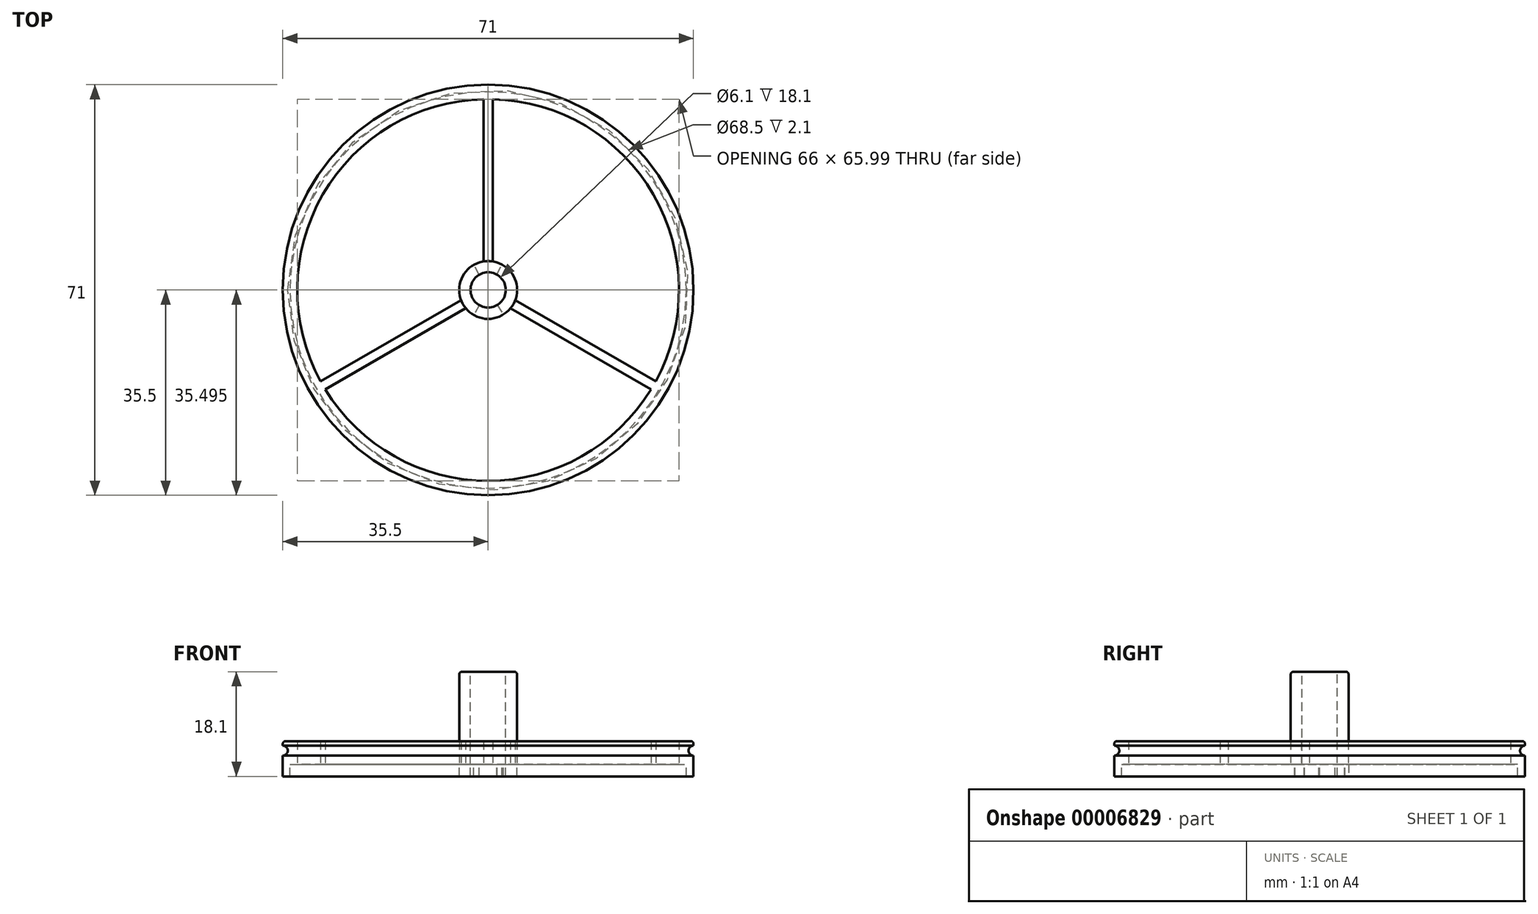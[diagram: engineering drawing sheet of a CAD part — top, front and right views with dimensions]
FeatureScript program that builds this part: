
annotation { "Feature Type Name" : "Feature", "Feature Type Description" : "" }
export const myFeature = defineFeature(function(context is Context, id is Id, definition is map)
    precondition{}
    {
        {
            var Q0;
            Q0=qCreatedBy(makeId("Top.planeOp"),FACE);
            var sketch = newSketch(context, id + "F0", { "sketchPlane" : qUnion([Q0])});
            skCircle(sketch, "E0", {"center": v(0, 0) * mm, "radius": 5 * mm});
            skCircle(sketch, "E1", {"center": v(0, 0) * mm, "radius": 33 * mm});
            skLineSegment(sketch, "E2", {"start": v(-0.81, 4.93) * mm, "end": v(-0.81, 33) * mm});
            skLineSegment(sketch, "E3.0.MirrorCS", {"start": v(0.81, 4.93) * mm, "end": v(0.81, 33) * mm});
            skLineSegment(sketch, "E4.1.0", {"start": v(-4.68, -1.76) * mm, "end": v(-28.98, -15.8) * mm});
            skLineSegment(sketch, "E4.1.1", {"start": v(-3.87, -3.17) * mm, "end": v(-28.16, -17.2) * mm});
            skLineSegment(sketch, "E4.2.0", {"start": v(3.87, -3.17) * mm, "end": v(28.16, -17.2) * mm});
            skLineSegment(sketch, "E4.2.1", {"start": v(4.68, -1.76) * mm, "end": v(28.98, -15.8) * mm});
            skCircle(sketch, "E5", {"center": v(0, 0) * mm, "radius": 35.5 * mm});
            skSolve(sketch);
        }
        {
            var Q0;
            Q0=makeQuery(id+"F0.imprint","IMPRINT",FACE,{"disambiguationData":[TD([[makeQuery(id+"F0.imprint","IMPRINT",EDGE,{"derivedFrom":sQuery(id+"F0.wireOp",EDGE,"E5")}),1.0]])]});
            var Q1;
            {var subQ1=sQuery(id+"F0.wireOp",EDGE,"E2");Q1=makeQuery(id+"F0.imprint","IMPRINT",FACE,{"disambiguationData":[TD([[makeQuery(id+"F0.imprint","IMPRINT",EDGE,{"derivedFrom":subQ1}),-1.0]])]});}
            var Q2;
            {var subQ0=sQuery(id+"F0.wireOp",EDGE,"E4.2.0");Q2=makeQuery(id+"F0.imprint","IMPRINT",FACE,{"disambiguationData":[TD([[makeQuery(id+"F0.imprint","IMPRINT",EDGE,{"derivedFrom":subQ0}),1.0]])]});}
            var Q3;
            {var subQ0=sQuery(id+"F0.wireOp",EDGE,"E4.1.0");Q3=makeQuery(id+"F0.imprint","IMPRINT",FACE,{"disambiguationData":[TD([[makeQuery(id+"F0.imprint","IMPRINT",EDGE,{"derivedFrom":subQ0}),1.0]])]});}
            var Q4;
            {var subQ0=sQuery(id+"F0.wireOp",EDGE,"E0");var subQ6=makeQuery(id+"F0.imprint","INTERSECT",VERTEX,{"derivedFrom":[subQ0,sQuery(id+"F0.wireOp",EDGE,"E2")]});Q4=makeQuery(id+"F0.imprint","IMPRINT",FACE,{"disambiguationData":[TD([[makeQuery(id+"F0.imprint","IMPRINT",EDGE,{"disambiguationData":[TD([[subQ6,1.0]])],"derivedFrom":subQ0}),1.0]])]});}
            extrude(context, id + "F1", {"entities" : qUnion([Q0, Q1, Q2, Q3, Q4]), "depth" : 4 * mm});
        }
        {
            var Q0;
            Q0=makeQuery(id+"F1.opExtrude","CAP_FACE",FACE,{"disambiguationData":[OSD([sQuery(id+"F0.wireOp",EDGE,"E0"),sQuery(id+"F0.wireOp",EDGE,"E1"),sQuery(id+"F0.wireOp",EDGE,"E2"),sQuery(id+"F0.wireOp",EDGE,"E3.0.MirrorCS"),sQuery(id+"F0.wireOp",EDGE,"E4.1.0"),sQuery(id+"F0.wireOp",EDGE,"E4.1.1"),sQuery(id+"F0.wireOp",EDGE,"E4.2.0"),sQuery(id+"F0.wireOp",EDGE,"E4.2.1"),sQuery(id+"F0.wireOp",EDGE,"E5")])],"isStart":false});
            var sketch = newSketch(context, id + "F2", { "sketchPlane" : qUnion([Q0])});
            skCircle(sketch, "E6", {"center": v(0, 0) * mm, "radius": 5 * mm});
            skSolve(sketch);
        }
        {
            var Q0;
            Q0 = qSketchRegion(id + "F2", true);
            extrude(context, id + "F3", {"entities" : qUnion([Q0]), "operationType" : NewBodyOperationType.ADD, "depth" : 12 * mm});
        }
        {
            var Q0;
            Q0=makeQuery(id+"F3.opExtrude","CAP_FACE",FACE,{"disambiguationData":[OSD([sQuery(id+"F2.wireOp",EDGE,"E6")])],"isStart":false});
            var sketch = newSketch(context, id + "F4", { "sketchPlane" : qUnion([Q0])});
            skCircle(sketch, "E7", {"center": v(0, 0) * mm, "radius": 3.05 * mm});
            skSolve(sketch);
        }
        {
            var Q0;
            Q0 = qSketchRegion(id + "F4", true);
            extrude(context, id + "F5", {"entities" : qUnion([Q0]), "operationType" : NewBodyOperationType.REMOVE, "endBound" : BoundingType.UP_TO_NEXT, "oppositeDirection" : true, "depth" : 25 * mm});
        }
        {
            var Q0;
            Q0=makeQuery(id+"F3.opExtrude","CAP_EDGE",EDGE,{"disambiguationData":[OSD([sQuery(id+"F2.wireOp",EDGE,"E6")])],"isStart":false});
            var Q1;
            Q1=makeQuery(id+"F1.opExtrude","CAP_EDGE",EDGE,{"disambiguationData":[OSD([sQuery(id+"F0.wireOp",EDGE,"E5")])],"isStart":false});
            fillet(context, id + "F6", {"entities" : qUnion([Q0, Q1]), "radius" : .5 * mm, "tangentPropagation" : true, "allowEdgeOverflow" : false});
        }
        {
            var Q0;
            Q0=makeQuery(id+"F1.opExtrude","CAP_FACE",FACE,{"disambiguationData":[OSD([sQuery(id+"F0.wireOp",EDGE,"E0"),sQuery(id+"F0.wireOp",EDGE,"E1"),sQuery(id+"F0.wireOp",EDGE,"E2"),sQuery(id+"F0.wireOp",EDGE,"E3.0.MirrorCS"),sQuery(id+"F0.wireOp",EDGE,"E4.1.0"),sQuery(id+"F0.wireOp",EDGE,"E4.1.1"),sQuery(id+"F0.wireOp",EDGE,"E4.2.0"),sQuery(id+"F0.wireOp",EDGE,"E4.2.1"),sQuery(id+"F0.wireOp",EDGE,"E5")])],"isStart":true});
            var sketch = newSketch(context, id + "F7", { "sketchPlane" : qUnion([Q0])});
            skCircle(sketch, "E8", {"center": v(0, 0) * mm, "radius": 35.5 * mm});
            skCircle(sketch, "E9", {"center": v(0, 0) * mm, "radius": 34.25 * mm});
            skLineSegment(sketch, "E10", {"start": v(3.05, 0) * mm, "end": v(5, 0) * mm});
            skLineSegment(sketch, "E11", {"start": v(1.56, 2.62) * mm, "end": v(2.62, 4.26) * mm});
            skLineSegment(sketch, "E12.1.0", {"start": v(-3.05, 0.04) * mm, "end": v(-5, 0.14) * mm});
            skLineSegment(sketch, "E12.1.1", {"start": v(-1.52, 2.64) * mm, "end": v(-2.5, 4.33) * mm});
            skLineSegment(sketch, "E12.2.0", {"start": v(1.49, -2.66) * mm, "end": v(2.38, -4.4) * mm});
            skLineSegment(sketch, "E12.2.1", {"start": v(-1.53, -2.64) * mm, "end": v(-2.5, -4.33) * mm});
            skArc(sketch, "E13", {"start": v(-2.5, 4.33) * mm, "mid": v(-4.3, 2.56) * mm, "end": v(-5, 0.14) * mm});
            skArc(sketch, "E14", {"start": v(5, 0) * mm, "mid": v(4.36, 2.44) * mm, "end": v(2.62, 4.26) * mm});
            skArc(sketch, "E15", {"start": v(-2.5, -4.33) * mm, "mid": v(-0.07, -5) * mm, "end": v(2.38, -4.4) * mm});
            skSolve(sketch);
        }
        {
            var Q0;
            {var subQ7=sQuery(id+"F7.wireOp",EDGE,"E10");Q0=makeQuery(id+"F7.imprint","IMPRINT",FACE,{"disambiguationData":[TD([[makeQuery(id+"F7.imprint","IMPRINT",EDGE,{"derivedFrom":subQ7}),1.0]])]});}
            var Q1;
            {var subQ7=sQuery(id+"F7.wireOp",EDGE,"E12.1.0");Q1=makeQuery(id+"F7.imprint","IMPRINT",FACE,{"disambiguationData":[TD([[makeQuery(id+"F7.imprint","IMPRINT",EDGE,{"derivedFrom":subQ7}),-1.0]])]});}
            var Q2;
            {var subQ7=sQuery(id+"F7.wireOp",EDGE,"E12.2.0");Q2=makeQuery(id+"F7.imprint","IMPRINT",FACE,{"disambiguationData":[TD([[makeQuery(id+"F7.imprint","IMPRINT",EDGE,{"derivedFrom":subQ7}),-1.0]])]});}
            var Q3;
            Q3=makeQuery(id+"F7.imprint","IMPRINT",FACE,{"disambiguationData":[TD([[makeQuery(id+"F7.imprint","IMPRINT",EDGE,{"derivedFrom":sQuery(id+"F7.wireOp",EDGE,"E8")}),-1.0]])]});
            extrude(context, id + "F8", {"entities" : qUnion([Q0, Q1, Q2, Q3]), "operationType" : NewBodyOperationType.ADD, "depth" : 2.1 * mm});
        }
        {
            var Q0;
            Q0=qCreatedBy(makeId("Front.planeOp"),FACE);
            var sketch = newSketch(context, id + "F9", { "sketchPlane" : qUnion([Q0])});
            skLineSegment(sketch, "E16", {"start": v(0, 24.07) * mm, "end": v(0, -11.35) * mm});
            skCircle(sketch, "E17", {"center": v(35.5, 2.35) * mm, "radius": 0.86 * mm});
            skSolve(sketch);
        }
        {
            var Q0;
            Q0=makeQuery(id+"F9.imprint","IMPRINT",FACE,{"disambiguationData":[TD([[makeQuery(id+"F9.imprint","IMPRINT",EDGE,{"derivedFrom":sQuery(id+"F9.wireOp",EDGE,"6bd00355-b684-466d-a8db-d7e66d906daf")}),1.0]])]});
            var Q1;
            Q1=makeQuery(id+"F9.imprint","IMPRINT",FACE,{"disambiguationData":[TD([[makeQuery(id+"F9.imprint","IMPRINT",EDGE,{"derivedFrom":sQuery(id+"F9.wireOp",EDGE,"E17")}),1.0]])]});
            var Q2;
            {var subQ0=sQuery(id+"F0.wireOp",EDGE,"E5");Q2=makeQuery(id+"F6.opFillet","BLEND_EDGE",EDGE,{"blendedFrom":[makeQuery(id+"F1.opExtrude","CAP_EDGE",EDGE,{"disambiguationData":[OSD([subQ0])],"isStart":false}),makeQuery(id+"F1.opExtrude","SWEPT_FACE",FACE,{"disambiguationData":[OSD([subQ0])]})],"blendedInto":[makeQuery(id+"F1.opExtrude","SWEPT_FACE",FACE,{"disambiguationData":[OSD([subQ0])]})]});}
            sweep(context, id + "F10", {"operationType" : NewBodyOperationType.REMOVE, "profiles" : qUnion([Q0, Q1]), "path" : qUnion([Q2])});
        }
    });
